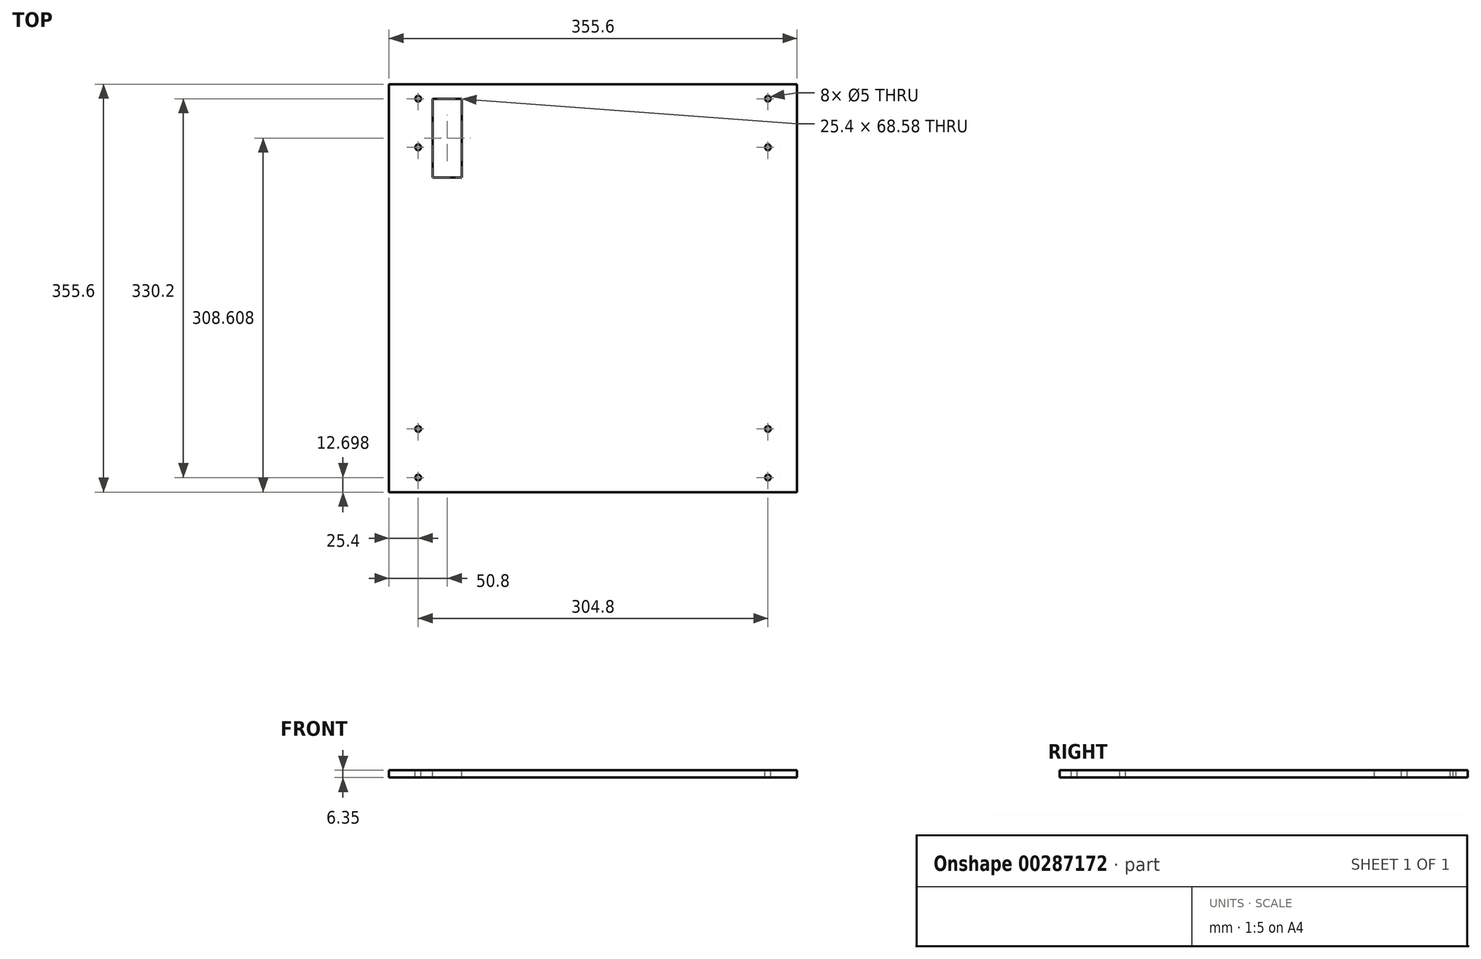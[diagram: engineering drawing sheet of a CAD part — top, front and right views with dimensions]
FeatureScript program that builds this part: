
annotation { "Feature Type Name" : "Feature", "Feature Type Description" : "" }
export const myFeature = defineFeature(function(context is Context, id is Id, definition is map)
    precondition{}
    {
        {
            var Q0;
            Q0=qCreatedBy(makeId("Top.planeOp"),FACE);
            var sketch = newSketch(context, id + "F0", { "sketchPlane" : qUnion([Q0])});
            skLineSegment(sketch, "E0.bottom", {"start": v(-311.9, 176.39) * mm, "end": v(43.7, 176.39) * mm});
            skLineSegment(sketch, "E0.top", {"start": v(-311.9, -179.21) * mm, "end": v(43.7, -179.21) * mm});
            skLineSegment(sketch, "E0.left", {"start": v(-311.9, 176.39) * mm, "end": v(-311.9, -179.21) * mm});
            skLineSegment(sketch, "E0.right", {"start": v(43.7, 176.39) * mm, "end": v(43.7, -179.21) * mm});
            skSolve(sketch);
        }
        {
            var Q0;
            Q0=makeQuery(id+"F0.imprint","IMPRINT",FACE,{"disambiguationData":[TD([[makeQuery(id+"F0.imprint","IMPRINT",EDGE,{"derivedFrom":sQuery(id+"F0.wireOp",EDGE,"E0.bottom")}),-1.0]])]});
            extrude(context, id + "F1", {"entities" : qUnion([Q0]), "depth" : 6.35 * mm});
        }
        {
            var Q0;
            Q0=makeQuery(id+"F1.opExtrude","CAP_FACE",FACE,{"disambiguationData":[OSD([sQuery(id+"F0.wireOp",EDGE,"E0.bottom"),sQuery(id+"F0.wireOp",EDGE,"E0.top"),sQuery(id+"F0.wireOp",EDGE,"E0.left"),sQuery(id+"F0.wireOp",EDGE,"E0.right")])],"isStart":false});
            var sketch = newSketch(context, id + "F2", { "sketchPlane" : qUnion([Q0])});
            skLineSegment(sketch, "E1", {"start": v(-286.5, 176.39) * mm, "end": v(-286.5, -179.21) * mm, "construction": true});
            skLineSegment(sketch, "E2", {"start": v(18.3, 176.39) * mm, "end": v(18.3, -179.21) * mm, "construction": true});
            skLineSegment(sketch, "E3", {"start": v(-311.9, -166.51) * mm, "end": v(43.7, -166.51) * mm, "construction": true});
            skLineSegment(sketch, "E4", {"start": v(-311.9, 163.69) * mm, "end": v(43.7, 163.69) * mm, "construction": true});
            skPoint(sketch, "E5", {"position": v(18.3, 163.69) * mm});
            skPoint(sketch, "E6", {"position": v(-286.5, 163.69) * mm});
            skPoint(sketch, "E7", {"position": v(-286.5, -166.51) * mm});
            skPoint(sketch, "E8", {"position": v(18.3, -166.51) * mm});
            skCircle(sketch, "E9", {"center": v(-286.5, 163.69) * mm, "radius": 2.5 * mm});
            skCircle(sketch, "E10", {"center": v(-286.5, -166.51) * mm, "radius": 2.5 * mm});
            skCircle(sketch, "E11", {"center": v(18.3, -166.51) * mm, "radius": 2.5 * mm});
            skCircle(sketch, "E12", {"center": v(18.3, 163.69) * mm, "radius": 2.5 * mm});
            skCircle(sketch, "E13", {"center": v(-286.5, -124.15) * mm, "radius": 2.5 * mm});
            skCircle(sketch, "E14", {"center": v(-286.5, 121.32) * mm, "radius": 2.5 * mm});
            skCircle(sketch, "E15", {"center": v(18.3, 121.32) * mm, "radius": 2.5 * mm});
            skCircle(sketch, "E16", {"center": v(18.3, -124.15) * mm, "radius": 2.5 * mm});
            skLineSegment(sketch, "E17.bottom", {"start": v(-273.8, 163.69) * mm, "end": v(-248.4, 163.69) * mm});
            skLineSegment(sketch, "E17.top", {"start": v(-273.8, 95.1) * mm, "end": v(-248.4, 95.1) * mm});
            skLineSegment(sketch, "E17.left", {"start": v(-273.8, 163.69) * mm, "end": v(-273.8, 95.1) * mm});
            skLineSegment(sketch, "E17.right", {"start": v(-248.4, 163.69) * mm, "end": v(-248.4, 95.1) * mm});
            skSolve(sketch);
        }
        {
            var Q0;
            Q0 = qSketchRegion(id + "F2", true);
            extrude(context, id + "F3", {"entities" : qUnion([Q0]), "operationType" : NewBodyOperationType.REMOVE, "endBound" : BoundingType.THROUGH_ALL, "oppositeDirection" : true, "depth" : 25.4 * mm});
        }
        {
            var Q0;
            Q0 = qSketchRegion(id + "F2", true);
            extrude(context, id + "F4", {"entities" : qUnion([Q0]), "operationType" : NewBodyOperationType.REMOVE, "endBound" : BoundingType.THROUGH_ALL, "oppositeDirection" : true, "depth" : 25.4 * mm});
        }
        {
            var Q0;
            Q0=makeQuery(id+"F2.imprint","IMPRINT",FACE,{"disambiguationData":[TD([[makeQuery(id+"F2.imprint","IMPRINT",EDGE,{"derivedFrom":sQuery(id+"F2.wireOp",EDGE,"E9")}),1.0]])]});
            var Q1;
            Q1=makeQuery(id+"F2.imprint","IMPRINT",FACE,{"disambiguationData":[TD([[makeQuery(id+"F2.imprint","IMPRINT",EDGE,{"derivedFrom":sQuery(id+"F2.wireOp",EDGE,"E10")}),1.0]])]});
            var Q2;
            Q2=makeQuery(id+"F2.imprint","IMPRINT",FACE,{"disambiguationData":[TD([[makeQuery(id+"F2.imprint","IMPRINT",EDGE,{"derivedFrom":sQuery(id+"F2.wireOp",EDGE,"E11")}),1.0]])]});
            var Q3;
            Q3=makeQuery(id+"F2.imprint","IMPRINT",FACE,{"disambiguationData":[TD([[makeQuery(id+"F2.imprint","IMPRINT",EDGE,{"derivedFrom":sQuery(id+"F2.wireOp",EDGE,"E12")}),1.0]])]});
            var Q4;
            Q4=makeQuery(id+"F2.imprint","IMPRINT",FACE,{"disambiguationData":[TD([[makeQuery(id+"F2.imprint","IMPRINT",EDGE,{"derivedFrom":sQuery(id+"F2.wireOp",EDGE,"E13")}),1.0]])]});
            var Q5;
            Q5=makeQuery(id+"F2.imprint","IMPRINT",FACE,{"disambiguationData":[TD([[makeQuery(id+"F2.imprint","IMPRINT",EDGE,{"derivedFrom":sQuery(id+"F2.wireOp",EDGE,"E14")}),1.0]])]});
            var Q6;
            Q6=makeQuery(id+"F2.imprint","IMPRINT",FACE,{"disambiguationData":[TD([[makeQuery(id+"F2.imprint","IMPRINT",EDGE,{"derivedFrom":sQuery(id+"F2.wireOp",EDGE,"E15")}),1.0]])]});
            var Q7;
            Q7=makeQuery(id+"F2.imprint","IMPRINT",FACE,{"disambiguationData":[TD([[makeQuery(id+"F2.imprint","IMPRINT",EDGE,{"derivedFrom":sQuery(id+"F2.wireOp",EDGE,"E16")}),1.0]])]});
            extrude(context, id + "F5", {"entities" : qUnion([Q0, Q1, Q2, Q3, Q4, Q5, Q6, Q7]), "operationType" : NewBodyOperationType.REMOVE, "endBound" : BoundingType.THROUGH_ALL, "oppositeDirection" : true, "depth" : 25.4 * mm});
        }
    });
